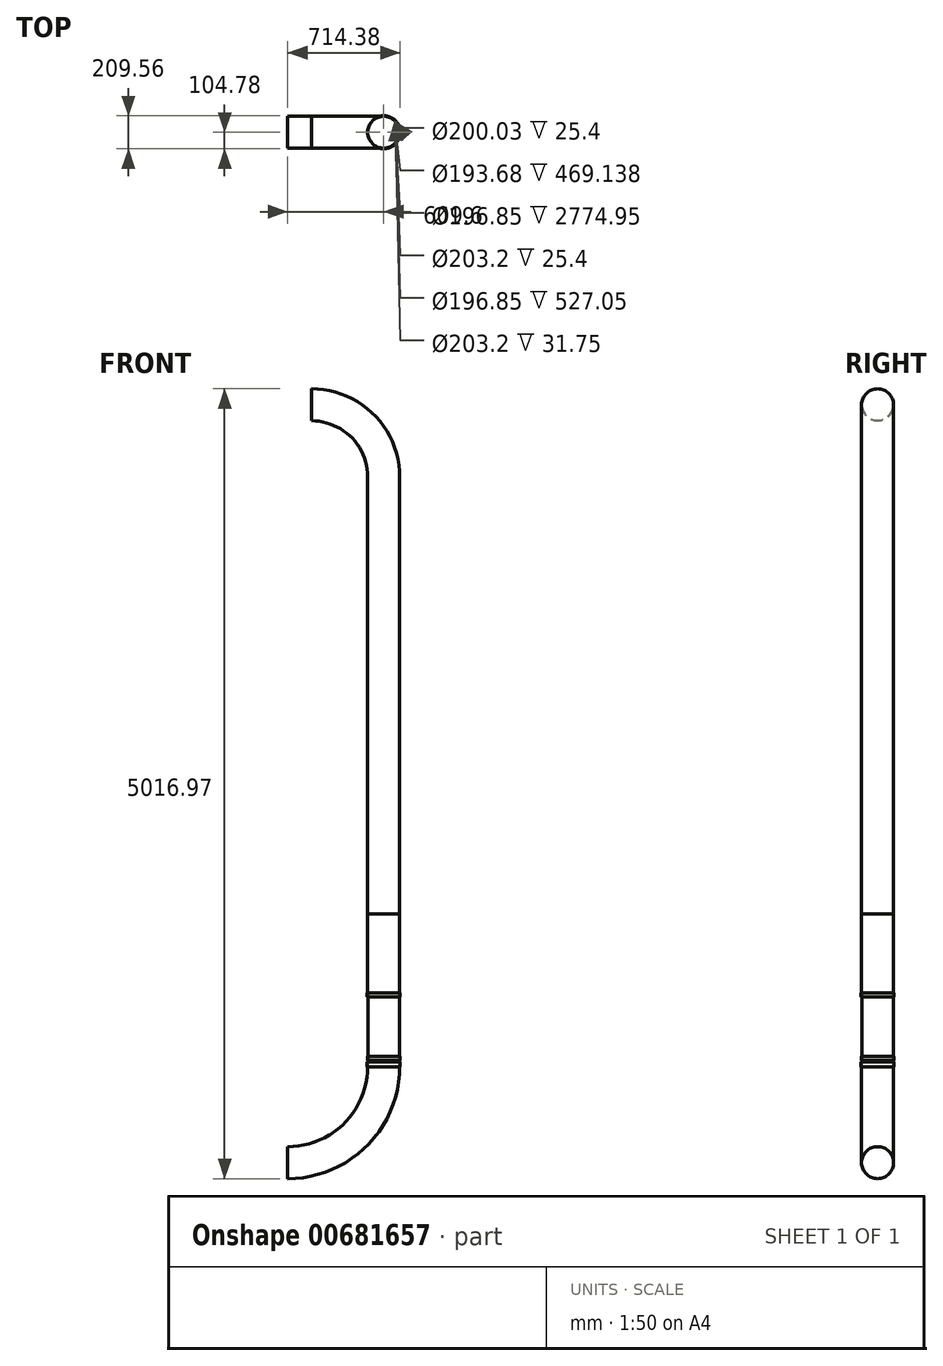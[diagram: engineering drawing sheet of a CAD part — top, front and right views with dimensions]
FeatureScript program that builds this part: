
annotation { "Feature Type Name" : "Feature", "Feature Type Description" : "" }
export const myFeature = defineFeature(function(context is Context, id is Id, definition is map)
    precondition{}
    {
        {
            var Q0;
            Q0=qCreatedBy(makeId("Front.planeOp"),FACE);
            var sketch = newSketch(context, id + "F0", { "sketchPlane" : qUnion([Q0])});
            skLineSegment(sketch, "E0", {"start": v(0, 0) * mm, "end": v(0, 1250.95) * mm, "construction": true});
            skLineSegment(sketch, "E1", {"start": v(0, 1250.95) * mm, "end": v(0, 1708.15) * mm, "construction": true});
            skLineSegment(sketch, "E2", {"start": v(0, 1708.15) * mm, "end": v(-457.2, 1708.15) * mm, "construction": true});
            skLineSegment(sketch, "E3", {"start": v(0, 0) * mm, "end": v(0, -1524) * mm, "construction": true});
            skLineSegment(sketch, "E4", {"start": v(0, -1524) * mm, "end": v(0, -2463.8) * mm, "construction": true});
            skLineSegment(sketch, "E5", {"start": v(0, -2463.8) * mm, "end": v(0, -3073.4) * mm, "construction": true});
            skLineSegment(sketch, "E6", {"start": v(0, -3073.4) * mm, "end": v(-609.6, -3073.4) * mm, "construction": true});
            skLineSegment(sketch, "E7", {"start": v(0, -2463.8) * mm, "end": v(-609.6, -2463.8) * mm, "construction": true});
            skLineSegment(sketch, "E8", {"start": v(0, -1524) * mm, "end": v(-101.6, -1524) * mm});
            skLineSegment(sketch, "E9", {"start": v(0, 1250.95) * mm, "end": v(-457.2, 1250.95) * mm, "construction": true});
            skLineSegment(sketch, "E10", {"start": v(0, -2025.65) * mm, "end": v(-203.2, -2025.65) * mm, "construction": true});
            skLineSegment(sketch, "E11", {"start": v(0, -2495.55) * mm, "end": v(-609.6, -2495.55) * mm, "construction": true});
            skLineSegment(sketch, "E12", {"start": v(0, -2051.05) * mm, "end": v(-203.2, -2051.05) * mm, "construction": true});
            skLineSegment(sketch, "E13", {"start": v(0, -2454.28) * mm, "end": v(-203.2, -2454.28) * mm, "construction": true});
            skSolve(sketch);
        }
        {
            var Q0;
            Q0=sQuery(id+"F0.wireOp",EDGE,"E7");
            cPlane(context, id + "F1", {"entities" : qUnion([Q0]), "cplaneType" : CPlaneType.LINE_ANGLE, "offset" : 25.4 * mm, "angle" : 90 * degree, "width" : 152.4 * mm, "height" : 152.4 * mm});
        }
        {
            var Q0;
            Q0=qCreatedBy(id+"F1.planeOp",FACE);
            var sketch = newSketch(context, id + "F2", { "sketchPlane" : qUnion([Q0])});
            skLineSegment(sketch, "E14", {"start": v(-609.6, 0) * mm, "end": v(-609.6, -203.2) * mm, "construction": true});
            skCircle(sketch, "E15", {"center": v(0, 0) * mm, "radius": 101.6 * mm});
            skCircle(sketch, "E16", {"center": v(0, 0) * mm, "radius": 104.78 * mm});
            skSolve(sketch);
        }
        {
            var Q0;
            Q0=sQuery(id+"F0.wireOp",EDGE,"E11");
            cPlane(context, id + "F3", {"entities" : qUnion([Q0]), "cplaneType" : CPlaneType.LINE_ANGLE, "offset" : 25.4 * mm, "angle" : 90 * degree, "width" : 152.4 * mm, "height" : 152.4 * mm});
        }
        {
            var Q0;
            Q0=qCreatedBy(id+"F3.planeOp",FACE);
            var sketch = newSketch(context, id + "F4", { "sketchPlane" : qUnion([Q0])});
            skLineSegment(sketch, "E17", {"start": v(-609.6, 0) * mm, "end": v(-609.6, -203.2) * mm, "construction": true});
            skCircle(sketch, "E18", {"center": v(0, 0) * mm, "radius": 101.6 * mm});
            skCircle(sketch, "E19", {"center": v(0, 0) * mm, "radius": 98.43 * mm});
            skSolve(sketch);
        }
        {
            var Q0;
            Q0=makeQuery(id+"F4.imprint","IMPRINT",FACE,{"disambiguationData":[TD([[makeQuery(id+"F4.imprint","IMPRINT",EDGE,{"derivedFrom":sQuery(id+"F4.wireOp",EDGE,"E18")}),1.0]])]});
            var Q1;
            Q1=sQuery(id+"F4.wireOp",EDGE,"E17");
            revolve(context, id + "F5", {"surfaceOperationType" : NewSurfaceOperationType.NEW, "entities" : qUnion([Q0]), "axis" : qUnion([Q1]), "revolveType" : RevolveType.ONE_DIRECTION, "oppositeDirection" : true, "angle" : 90 * degree});
        }
        {
            var Q0;
            Q0=sQuery(id+"F0.wireOp",EDGE,"E12");
            cPlane(context, id + "F6", {"entities" : qUnion([Q0]), "cplaneType" : CPlaneType.LINE_ANGLE, "offset" : 25.4 * mm, "angle" : 90 * degree, "width" : 152.4 * mm, "height" : 152.4 * mm});
        }
        {
            var Q0;
            Q0=makeQuery(id+"F2.imprint","IMPRINT",FACE,{"disambiguationData":[TD([[makeQuery(id+"F2.imprint","IMPRINT",EDGE,{"derivedFrom":sQuery(id+"F2.wireOp",EDGE,"E15")}),-1.0]])]});
            extrude(context, id + "F7", {"entities" : qUnion([Q0]), "oppositeDirection" : true, "depth" : 31.75 * mm, "offsetDistance" : 25.4 * mm});
        }
        {
            var Q0;
            Q0=qCreatedBy(id+"F6.planeOp",FACE);
            var sketch = newSketch(context, id + "F8", { "sketchPlane" : qUnion([Q0])});
            skCircle(sketch, "E20", {"center": v(0, 0) * mm, "radius": 101.6 * mm});
            skCircle(sketch, "E21", {"center": v(0, 0) * mm, "radius": 104.78 * mm});
            skSolve(sketch);
        }
        {
            var Q0;
            Q0 = qSketchRegion(id + "F8", true);
            extrude(context, id + "F9", {"entities" : qUnion([Q0]), "depth" : 25.4 * mm, "offsetDistance" : 25.4 * mm});
        }
        {
            var Q0;
            Q0=qCreatedBy(id+"F3.planeOp",FACE);
            var sketch = newSketch(context, id + "F10", { "sketchPlane" : qUnion([Q0])});
            skCircle(sketch, "E22", {"center": v(0, 0) * mm, "radius": 100.01 * mm});
            skCircle(sketch, "E23", {"center": v(0, 0) * mm, "radius": 96.84 * mm});
            skSolve(sketch);
        }
        {
            var Q0;
            Q0=makeQuery(id+"F10.imprint","IMPRINT",FACE,{"disambiguationData":[TD([[makeQuery(id+"F10.imprint","IMPRINT",EDGE,{"derivedFrom":sQuery(id+"F10.wireOp",EDGE,"E22")}),1.0]])]});
            extrude(context, id + "F11", {"entities" : qUnion([Q0]), "depth" : 469.14 * mm, "offsetDistance" : 25.4 * mm});
        }
        {
            var Q0;
            Q0=sQuery(id+"F0.wireOp",EDGE,"E13");
            cPlane(context, id + "F12", {"entities" : qUnion([Q0]), "cplaneType" : CPlaneType.LINE_ANGLE, "offset" : 25.4 * mm, "angle" : 90 * degree, "width" : 152.4 * mm, "height" : 152.4 * mm});
        }
        {
            var Q0;
            Q0=qCreatedBy(id+"F12.planeOp",FACE);
            var sketch = newSketch(context, id + "F13", { "sketchPlane" : qUnion([Q0])});
            skCircle(sketch, "E24", {"center": v(0, 0) * mm, "radius": 100.01 * mm});
            skCircle(sketch, "E25", {"center": v(0, 0) * mm, "radius": 103.19 * mm});
            skSolve(sketch);
        }
        {
            var Q0;
            Q0=makeQuery(id+"F13.imprint","IMPRINT",FACE,{"disambiguationData":[TD([[makeQuery(id+"F13.imprint","IMPRINT",EDGE,{"derivedFrom":sQuery(id+"F13.wireOp",EDGE,"E24")}),-1.0]])]});
            extrude(context, id + "F14", {"entities" : qUnion([Q0]), "depth" : 25.4 * mm, "offsetDistance" : 25.4 * mm});
        }
        {
            var Q0;
            Q0=qCreatedBy(id+"F6.planeOp",FACE);
            var sketch = newSketch(context, id + "F15", { "sketchPlane" : qUnion([Q0])});
            skCircle(sketch, "E26", {"center": v(0, 0) * mm, "radius": 101.6 * mm});
            skCircle(sketch, "E27", {"center": v(0, 0) * mm, "radius": 98.43 * mm});
            skSolve(sketch);
        }
        {
            var Q0;
            Q0=makeQuery(id+"F15.imprint","IMPRINT",FACE,{"disambiguationData":[TD([[makeQuery(id+"F15.imprint","IMPRINT",EDGE,{"derivedFrom":sQuery(id+"F15.wireOp",EDGE,"E26")}),1.0]])]});
            extrude(context, id + "F16", {"entities" : qUnion([Q0]), "depth" : 527.05 * mm, "offsetDistance" : 25.4 * mm});
        }
        {
            var Q0;
            Q0=sQuery(id+"F0.wireOp",EDGE,"E8");
            cPlane(context, id + "F17", {"entities" : qUnion([Q0]), "cplaneType" : CPlaneType.LINE_ANGLE, "offset" : 25.4 * mm, "angle" : 90 * degree, "width" : 152.4 * mm, "height" : 152.4 * mm});
        }
        {
            var Q0;
            Q0=qCreatedBy(id+"F17.planeOp",FACE);
            var sketch = newSketch(context, id + "F18", { "sketchPlane" : qUnion([Q0])});
            skCircle(sketch, "E28", {"center": v(0, 0) * mm, "radius": 101.6 * mm});
            skCircle(sketch, "E29", {"center": v(0, 0) * mm, "radius": 98.43 * mm});
            skSolve(sketch);
        }
        {
            var Q0;
            Q0=makeQuery(id+"F18.imprint","IMPRINT",FACE,{"disambiguationData":[TD([[makeQuery(id+"F18.imprint","IMPRINT",EDGE,{"derivedFrom":sQuery(id+"F18.wireOp",EDGE,"E28")}),1.0]])]});
            extrude(context, id + "F19", {"entities" : qUnion([Q0]), "depth" : 1524 * mm, "offsetDistance" : 25.4 * mm});
        }
        {
            var Q0;
            Q0=qCreatedBy(makeId("Top.planeOp"),FACE);
            var sketch = newSketch(context, id + "F20", { "sketchPlane" : qUnion([Q0])});
            skCircle(sketch, "E30", {"center": v(0, 0) * mm, "radius": 101.6 * mm});
            skCircle(sketch, "E31", {"center": v(0, 0) * mm, "radius": 98.43 * mm});
            skSolve(sketch);
        }
        {
            var Q0;
            Q0=sQuery(id+"F0.wireOp",EDGE,"E9");
            cPlane(context, id + "F21", {"entities" : qUnion([Q0]), "cplaneType" : CPlaneType.LINE_ANGLE, "offset" : 25.4 * mm, "angle" : 90 * degree, "width" : 152.4 * mm, "height" : 152.4 * mm});
        }
        {
            var Q0;
            Q0=qCreatedBy(id+"F21.planeOp",FACE);
            var sketch = newSketch(context, id + "F22", { "sketchPlane" : qUnion([Q0])});
            skLineSegment(sketch, "E32", {"start": v(-186274.22, 0) * mm, "end": v(-186274.22, -203.2) * mm});
            skLineSegment(sketch, "E33", {"start": v(-457.67, 0) * mm, "end": v(-457.67, -203.2) * mm, "construction": true});
            skCircle(sketch, "E34", {"center": v(0, 0) * mm, "radius": 101.6 * mm});
            skCircle(sketch, "E35", {"center": v(0, 0) * mm, "radius": 98.43 * mm});
            skSolve(sketch);
        }
        {
            var Q0;
            Q0=makeQuery(id+"F22.imprint","IMPRINT",FACE,{"disambiguationData":[TD([[makeQuery(id+"F22.imprint","IMPRINT",EDGE,{"derivedFrom":sQuery(id+"F22.wireOp",EDGE,"E34")}),1.0]])]});
            var Q1;
            Q1=sQuery(id+"F22.wireOp",EDGE,"E33");
            revolve(context, id + "F23", {"surfaceOperationType" : NewSurfaceOperationType.NEW, "entities" : qUnion([Q0]), "axis" : qUnion([Q1]), "revolveType" : RevolveType.ONE_DIRECTION, "angle" : 90 * degree});
        }
        {
            var Q0;
            Q0=makeQuery(id+"F20.imprint","IMPRINT",FACE,{"disambiguationData":[TD([[makeQuery(id+"F20.imprint","IMPRINT",EDGE,{"derivedFrom":sQuery(id+"F20.wireOp",EDGE,"E30")}),1.0]])]});
            extrude(context, id + "F24", {"entities" : qUnion([Q0]), "operationType" : NewBodyOperationType.ADD, "depth" : 1250.95 * mm, "offsetDistance" : 25.4 * mm});
        }
    });
